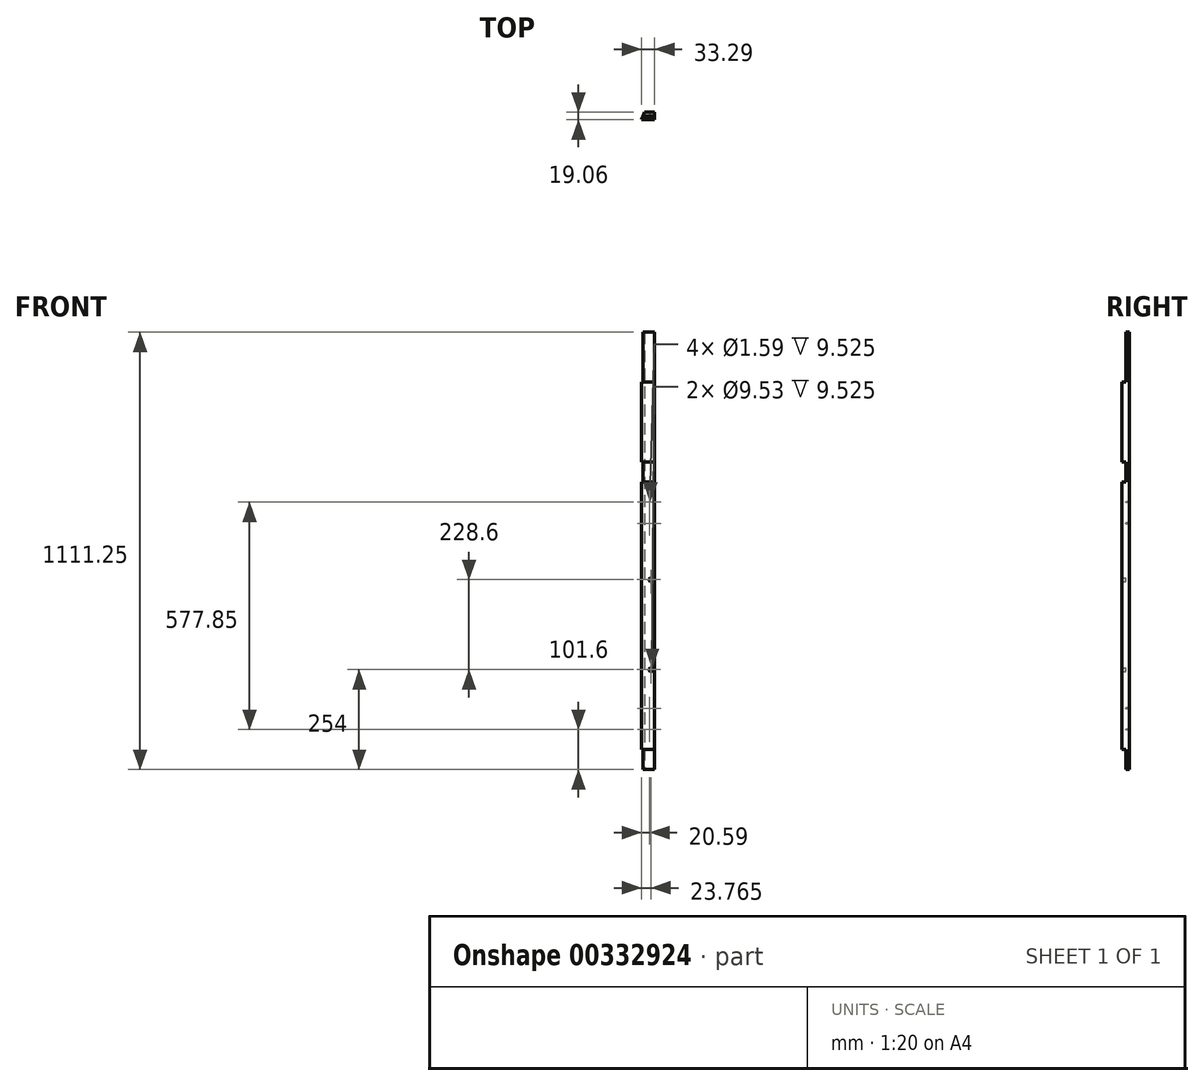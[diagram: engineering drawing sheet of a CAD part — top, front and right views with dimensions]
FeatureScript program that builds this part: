
annotation { "Feature Type Name" : "Feature", "Feature Type Description" : "" }
export const myFeature = defineFeature(function(context is Context, id is Id, definition is map)
    precondition{}
    {
        {
            var Q0;
            Q0=qCreatedBy(makeId("Top.planeOp"),FACE);
            var sketch = newSketch(context, id + "F0", { "sketchPlane" : qUnion([Q0])});
            skLineSegment(sketch, "E0.bottom", {"start": v(25.4, 9.53) * mm, "end": v(0, 9.53) * mm});
            skLineSegment(sketch, "E0.top", {"start": v(25.4, -9.53) * mm, "end": v(-7.9, -9.53) * mm});
            skLineSegment(sketch, "E0.left", {"start": v(25.4, 9.53) * mm, "end": v(25.4, -9.52) * mm});
            skPoint(sketch, "E0.middle", {"position": v(0, 0) * mm});
            skLineSegment(sketch, "E1", {"start": v(0, 9.53) * mm, "end": v(-7.9, -9.52) * mm});
            skPoint(sketch, "E0.right.end.orphan", {"position": v(-25.4, -9.53) * mm});
            skPoint(sketch, "E2.orphan", {"position": v(-25.4, 9.53) * mm});
            skSolve(sketch);
        }
        {
            var Q0;
            Q0=makeQuery(id+"F0.imprint","IMPRINT",FACE,{"disambiguationData":[TD([[makeQuery(id+"F0.imprint","IMPRINT",EDGE,{"derivedFrom":sQuery(id+"F0.wireOp",EDGE,"E0.bottom")}),1.0]])]});
            extrude(context, id + "F1", {"entities" : qUnion([Q0]), "depth" : 1111.25 * mm});
        }
        {
            var Q0;
            Q0=qCreatedBy(makeId("Front.planeOp"),FACE);
            var sketch = newSketch(context, id + "F2", { "sketchPlane" : qUnion([Q0])});
            skLineSegment(sketch, "E3.bottom", {"start": v(-38.77, 0) * mm, "end": v(83.66, 0) * mm});
            skLineSegment(sketch, "E3.top", {"start": v(-38.77, 50.8) * mm, "end": v(83.66, 50.8) * mm});
            skLineSegment(sketch, "E3.left", {"start": v(-38.77, 0) * mm, "end": v(-38.77, 50.8) * mm});
            skLineSegment(sketch, "E3.right", {"start": v(83.66, 0) * mm, "end": v(83.66, 50.8) * mm});
            skLineSegment(sketch, "E4.bottom", {"start": v(-44.21, 730.25) * mm, "end": v(49.65, 730.25) * mm});
            skLineSegment(sketch, "E4.top", {"start": v(-44.21, 781.05) * mm, "end": v(49.65, 781.05) * mm});
            skLineSegment(sketch, "E4.left", {"start": v(-44.21, 730.25) * mm, "end": v(-44.21, 781.05) * mm});
            skLineSegment(sketch, "E4.right", {"start": v(49.65, 730.25) * mm, "end": v(49.65, 781.05) * mm});
            skLineSegment(sketch, "E5.bottom", {"start": v(-210.36, 984.25) * mm, "end": v(132.8, 984.25) * mm});
            skLineSegment(sketch, "E5.top", {"start": v(-210.36, 1111.25) * mm, "end": v(132.8, 1111.25) * mm});
            skLineSegment(sketch, "E5.left", {"start": v(-210.36, 984.25) * mm, "end": v(-210.36, 1111.25) * mm});
            skLineSegment(sketch, "E5.right", {"start": v(132.8, 984.25) * mm, "end": v(132.8, 1111.25) * mm});
            skSolve(sketch);
        }
        {
            var Q0;
            Q0=qSketchRegion(id+"F2",true);
            extrude(context, id + "F3", {"entities" : qUnion([Q0]), "operationType" : NewBodyOperationType.REMOVE, "depth" : 25.4 * mm});
        }
        {
            var Q0;
            Q0=qCreatedBy(makeId("Front.planeOp"),FACE);
            var sketch = newSketch(context, id + "F4", { "sketchPlane" : qUnion([Q0])});
            skCircle(sketch, "E6", {"center": v(12.7, 101.6) * mm, "radius": 0.8 * mm});
            skCircle(sketch, "E7", {"center": v(12.7, 155.58) * mm, "radius": 0.8 * mm});
            skCircle(sketch, "E8", {"center": v(12.7, 625.48) * mm, "radius": 0.8 * mm});
            skCircle(sketch, "E9", {"center": v(12.7, 679.45) * mm, "radius": 0.8 * mm});
            skLineSegment(sketch, "E10", {"start": v(0, 0) * mm, "end": v(0, 1192.46) * mm, "construction": true});
            skLineSegment(sketch, "E11.bottom", {"start": v(12.7, 101.6) * mm, "end": v(-12.7, 101.6) * mm, "construction": true});
            skLineSegment(sketch, "E11.top", {"start": v(12.7, 679.45) * mm, "end": v(-12.7, 679.45) * mm, "construction": true});
            skLineSegment(sketch, "E11.left", {"start": v(12.7, 101.6) * mm, "end": v(12.7, 679.45) * mm, "construction": true});
            skLineSegment(sketch, "E11.right", {"start": v(-12.7, 101.6) * mm, "end": v(-12.7, 679.45) * mm, "construction": true});
            skCircle(sketch, "E12", {"center": v(-12.7, 625.48) * mm, "radius": 0.8 * mm});
            skCircle(sketch, "E13", {"center": v(-12.7, 679.45) * mm, "radius": 0.8 * mm});
            skCircle(sketch, "E14", {"center": v(-12.7, 101.6) * mm, "radius": 0.8 * mm});
            skCircle(sketch, "E15", {"center": v(-12.7, 155.58) * mm, "radius": 0.8 * mm});
            skSolve(sketch);
        }
        {
            var Q0;
            Q0=qSketchRegion(id+"F4",true);
            extrude(context, id + "F5", {"entities" : qUnion([Q0]), "operationType" : NewBodyOperationType.REMOVE, "oppositeDirection" : true, "depth" : 25.4 * mm});
        }
        {
            var Q0;
            Q0=qCreatedBy(makeId("Front.planeOp"),FACE);
            var sketch = newSketch(context, id + "F6", { "sketchPlane" : qUnion([Q0])});
            skCircle(sketch, "E16", {"center": v(15.88, 254) * mm, "radius": 4.76 * mm});
            skCircle(sketch, "E17", {"center": v(15.87, 482.6) * mm, "radius": 4.76 * mm});
            skSolve(sketch);
        }
        {
            var Q0;
            Q0=qSketchRegion(id+"F6",true);
            extrude(context, id + "F7", {"entities" : qUnion([Q0]), "operationType" : NewBodyOperationType.REMOVE, "depth" : 25.4 * mm});
        }
    });
